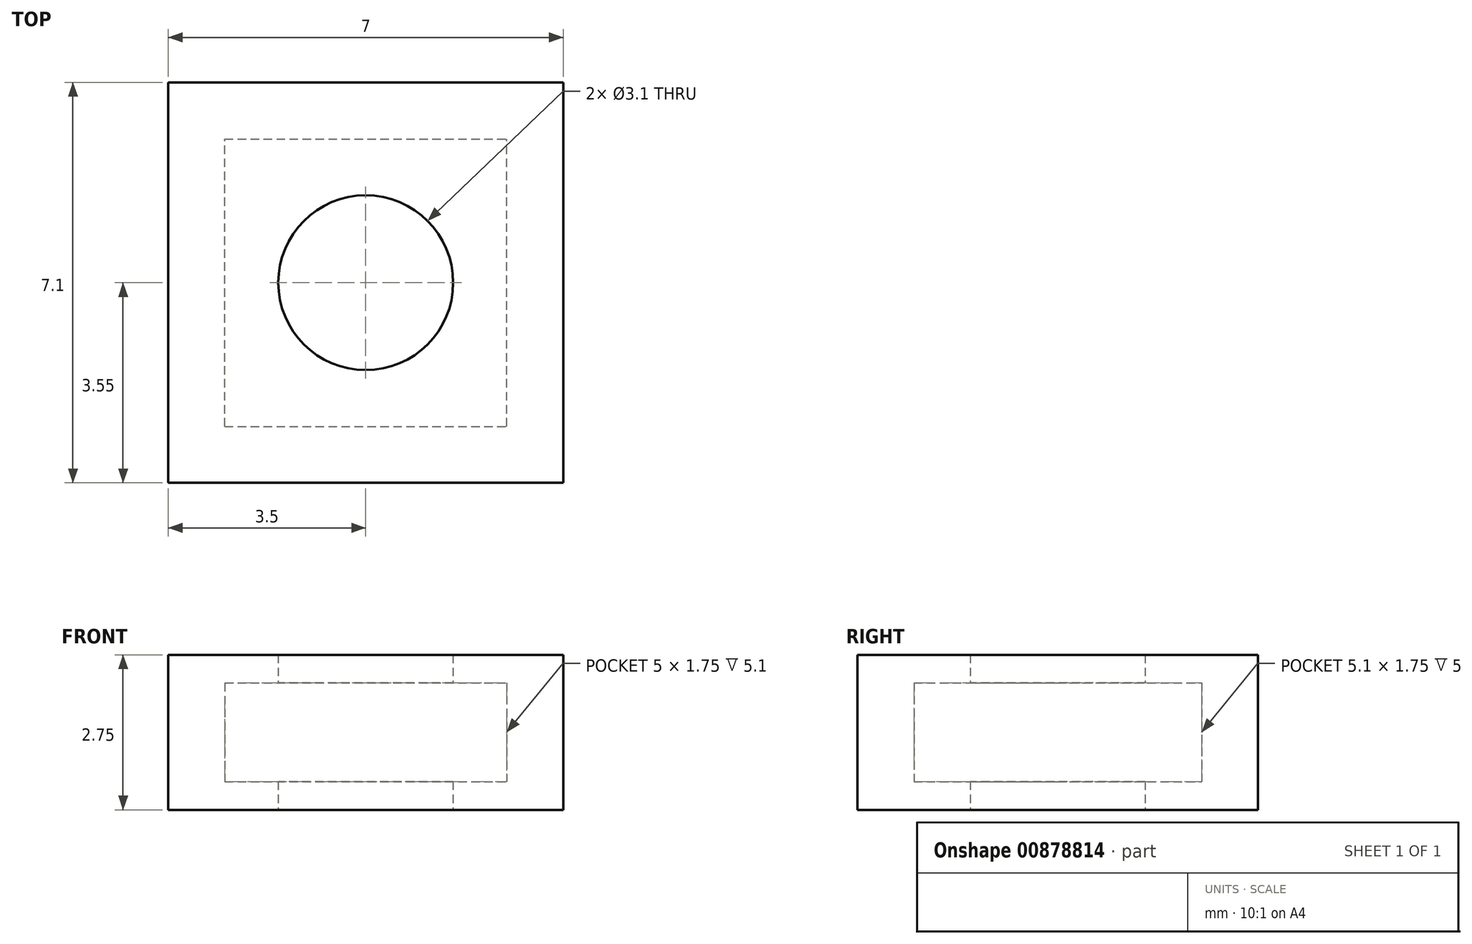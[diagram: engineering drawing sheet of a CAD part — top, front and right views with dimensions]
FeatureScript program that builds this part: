
annotation { "Feature Type Name" : "Feature", "Feature Type Description" : "" }
export const myFeature = defineFeature(function(context is Context, id is Id, definition is map)
    precondition{}
    {
        {
            var Q0;
            Q0=qCreatedBy(makeId("Top.planeOp"),FACE);
            var sketch = newSketch(context, id + "F0", { "sketchPlane" : qUnion([Q0])});
            skCircle(sketch, "E0", {"center": v(0, 0) * mm, "radius": 2.5 * mm, "construction": true});
            skLineSegment(sketch, "E1.bottom", {"start": v(-2.5, -2.55) * mm, "end": v(2.5, -2.55) * mm, "construction": true});
            skLineSegment(sketch, "E1.top", {"start": v(-2.5, 2.55) * mm, "end": v(2.5, 2.55) * mm, "construction": true});
            skLineSegment(sketch, "E1.left", {"start": v(-2.5, -2.55) * mm, "end": v(-2.5, 2.55) * mm, "construction": true});
            skLineSegment(sketch, "E1.right", {"start": v(2.5, -2.55) * mm, "end": v(2.5, 2.55) * mm, "construction": true});
            skLineSegment(sketch, "E2.0", {"start": v(-3.5, 3.55) * mm, "end": v(3.5, 3.55) * mm});
            skLineSegment(sketch, "E2.1", {"start": v(-3.5, -3.55) * mm, "end": v(-3.5, 3.55) * mm});
            skLineSegment(sketch, "E2.2", {"start": v(-3.5, -3.55) * mm, "end": v(3.5, -3.55) * mm});
            skLineSegment(sketch, "E2.3", {"start": v(3.5, -3.55) * mm, "end": v(3.5, 3.55) * mm});
            skCircle(sketch, "E3", {"center": v(0, 0) * mm, "radius": 1.55 * mm});
            skLineSegment(sketch, "E4", {"start": v(0, 0) * mm, "end": v(4.4, 0) * mm, "construction": true});
            skSolve(sketch);
        }
        {
            var Q0;
            Q0 = qSketchRegion(id + "F0", true);
            extrude(context, id + "F1", {"entities" : qUnion([Q0]), "depth" : .5 * mm, "offsetDistance" : 25 * mm});
        }
        {
            var Q0;
            Q0=makeQuery(id+"F1.opExtrude","CAP_FACE",FACE,{"disambiguationData":[OSD([sQuery(id+"F0.wireOp",EDGE,"E2.0"),sQuery(id+"F0.wireOp",EDGE,"E2.1"),sQuery(id+"F0.wireOp",EDGE,"E2.2"),sQuery(id+"F0.wireOp",EDGE,"E2.3")])],"isStart":false});
            var sketch = newSketch(context, id + "F2", { "sketchPlane" : qUnion([Q0])});
            skLineSegment(sketch, "E5.0", {"start": v(-3.5, 3.55) * mm, "end": v(3.5, 3.55) * mm});
            skLineSegment(sketch, "E5.1", {"start": v(3.5, -3.55) * mm, "end": v(3.5, 3.55) * mm});
            skLineSegment(sketch, "E5.2", {"start": v(-3.5, -3.55) * mm, "end": v(3.5, -3.55) * mm});
            skLineSegment(sketch, "E5.3", {"start": v(-3.5, -3.55) * mm, "end": v(-3.5, 3.55) * mm});
            skLineSegment(sketch, "E6.0", {"start": v(-2.5, 2.55) * mm, "end": v(2.5, 2.55) * mm});
            skLineSegment(sketch, "E6.1", {"start": v(-2.5, -2.55) * mm, "end": v(-2.5, 2.55) * mm});
            skLineSegment(sketch, "E6.2", {"start": v(-2.5, -2.55) * mm, "end": v(2.5, -2.55) * mm});
            skLineSegment(sketch, "E6.3", {"start": v(2.5, -2.55) * mm, "end": v(2.5, 2.55) * mm});
            skSolve(sketch);
        }
        {
            var Q0;
            Q0 = qSketchRegion(id + "F2", true);
            extrude(context, id + "F3", {"entities" : qUnion([Q0]), "operationType" : NewBodyOperationType.ADD, "depth" : 1.75 * mm, "offsetDistance" : 25 * mm});
        }
        {
            var Q0;
            Q0=makeQuery(id+"F3.opExtrude","CAP_FACE",FACE,{"disambiguationData":[OSD([sQuery(id+"F2.wireOp",EDGE,"E5.0"),sQuery(id+"F2.wireOp",EDGE,"E5.1"),sQuery(id+"F2.wireOp",EDGE,"E5.2"),sQuery(id+"F2.wireOp",EDGE,"E5.3"),sQuery(id+"F2.wireOp",EDGE,"E6.0"),sQuery(id+"F2.wireOp",EDGE,"E6.1"),sQuery(id+"F2.wireOp",EDGE,"E6.2"),sQuery(id+"F2.wireOp",EDGE,"E6.3")])],"isStart":false});
            var sketch = newSketch(context, id + "F4", { "sketchPlane" : qUnion([Q0])});
            skLineSegment(sketch, "E7.0", {"start": v(-3.5, 3.55) * mm, "end": v(3.5, 3.55) * mm});
            skLineSegment(sketch, "E7.1", {"start": v(-3.5, -3.55) * mm, "end": v(-3.5, 3.55) * mm});
            skLineSegment(sketch, "E7.2", {"start": v(-3.5, -3.55) * mm, "end": v(3.5, -3.55) * mm});
            skLineSegment(sketch, "E7.3", {"start": v(3.5, -3.55) * mm, "end": v(3.5, 3.55) * mm});
            skCircle(sketch, "E8.0", {"center": v(0, 0) * mm, "radius": 1.55 * mm});
            skSolve(sketch);
        }
        {
            var Q0;
            Q0 = qSketchRegion(id + "F4", true);
            extrude(context, id + "F5", {"entities" : qUnion([Q0]), "operationType" : NewBodyOperationType.ADD, "depth" : .5 * mm, "offsetDistance" : 25 * mm});
        }
    });
